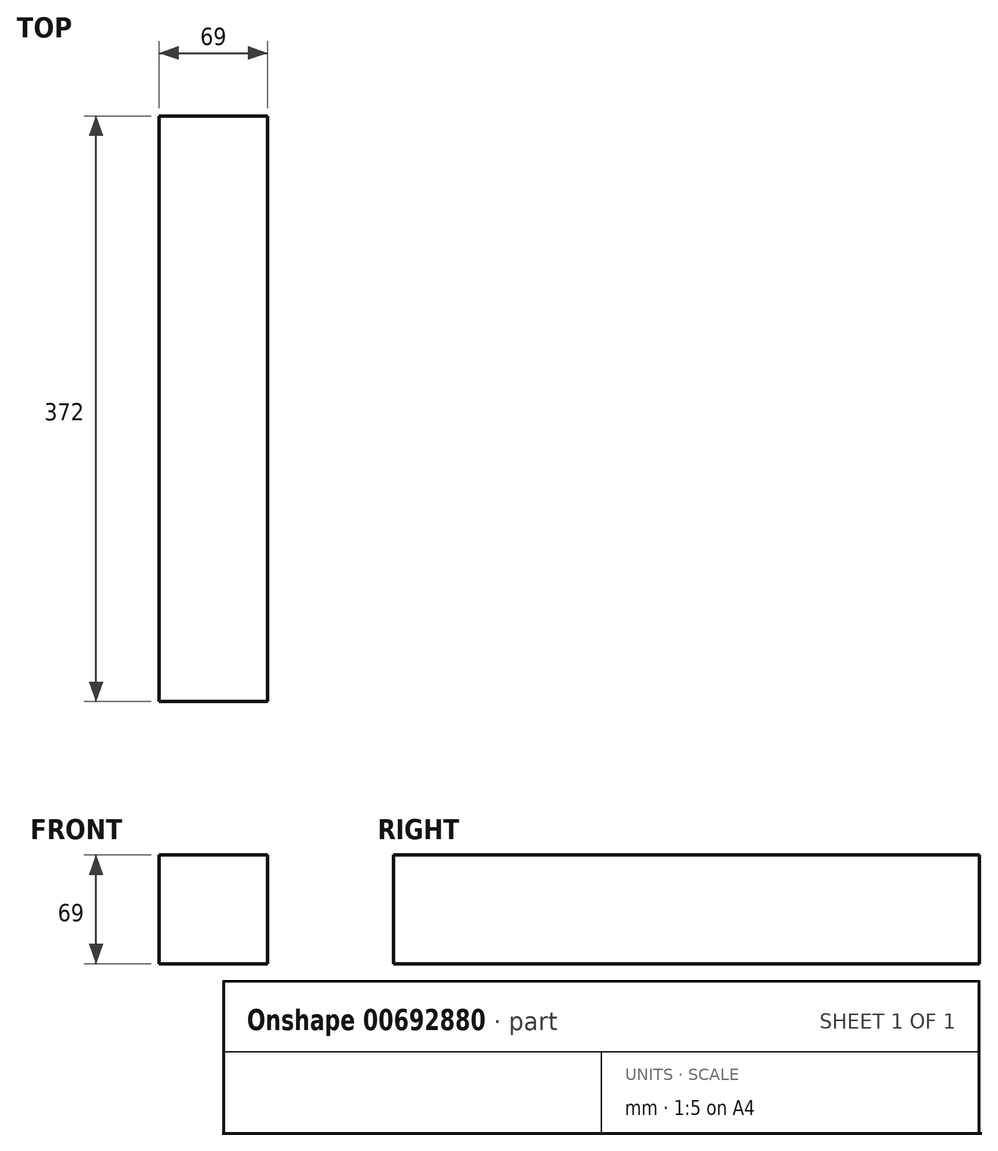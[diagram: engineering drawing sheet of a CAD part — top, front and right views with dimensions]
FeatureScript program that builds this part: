
annotation { "Feature Type Name" : "Feature", "Feature Type Description" : "" }
export const myFeature = defineFeature(function(context is Context, id is Id, definition is map)
    precondition{}
    {
        {
            var Q0;
            Q0=qCreatedBy(makeId("Front.planeOp"),FACE);
            var sketch = newSketch(context, id + "F0", { "sketchPlane" : qUnion([Q0])});
            skLineSegment(sketch, "E0.bottom", {"start": v(34.5, 34.5) * mm, "end": v(-34.5, 34.5) * mm});
            skLineSegment(sketch, "E0.top", {"start": v(34.5, -34.5) * mm, "end": v(-34.5, -34.5) * mm});
            skLineSegment(sketch, "E0.left", {"start": v(34.5, 34.5) * mm, "end": v(34.5, -34.5) * mm});
            skLineSegment(sketch, "E0.right", {"start": v(-34.5, 34.5) * mm, "end": v(-34.5, -34.5) * mm});
            skPoint(sketch, "E0.middle", {"position": v(0, 0) * mm});
            skSolve(sketch);
        }
        {
            var Q0;
            Q0 = qSketchRegion(id + "F0", true);
            extrude(context, id + "F1", {"entities" : qUnion([Q0]), "oppositeDirection" : true, "depth" : 372 * mm, "offsetDistance" : 25 * mm});
        }
    });
